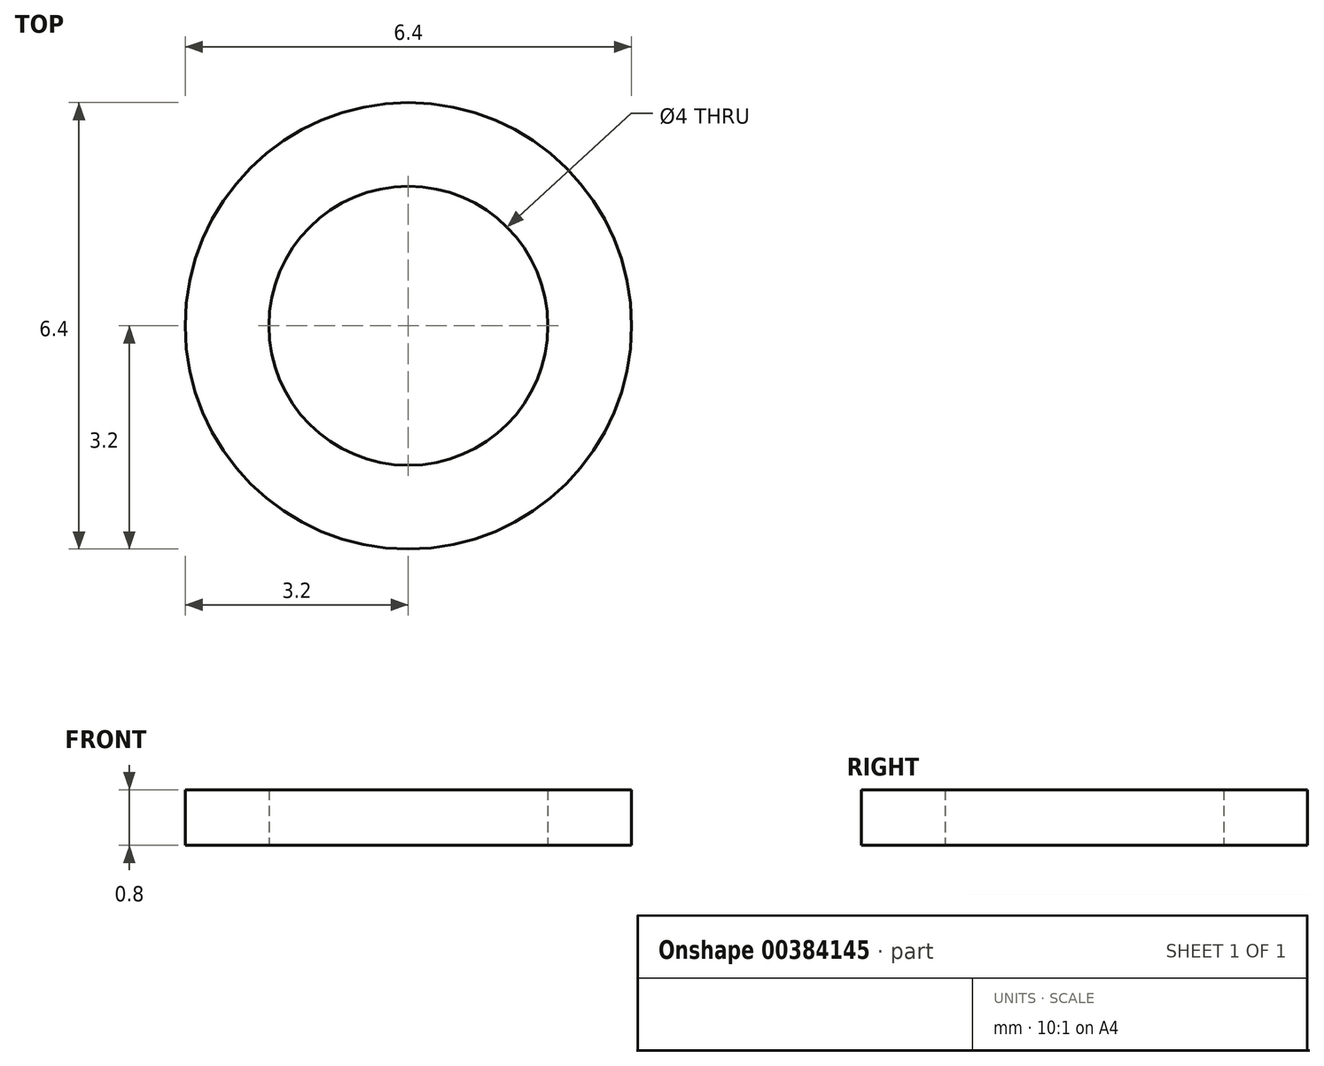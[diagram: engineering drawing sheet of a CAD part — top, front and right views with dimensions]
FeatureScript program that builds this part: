
annotation { "Feature Type Name" : "Feature", "Feature Type Description" : "" }
export const myFeature = defineFeature(function(context is Context, id is Id, definition is map)
    precondition{}
    {
        {
            var Q0;
            Q0=qCreatedBy(makeId("Top.planeOp"),FACE);
            var sketch = newSketch(context, id + "F0", { "sketchPlane" : qUnion([Q0])});
            skCircle(sketch, "E0", {"center": v(0, 0) * mm, "radius": 3.2 * mm});
            skCircle(sketch, "E1", {"center": v(0, 0) * mm, "radius": 2 * mm});
            skSolve(sketch);
        }
        {
            var Q0;
            Q0 = qSketchRegion(id + "F0", true);
            extrude(context, id + "F1", {"entities" : qUnion([Q0]), "depth" : .8 * mm, "offsetDistance" : 25 * mm});
        }
    });
